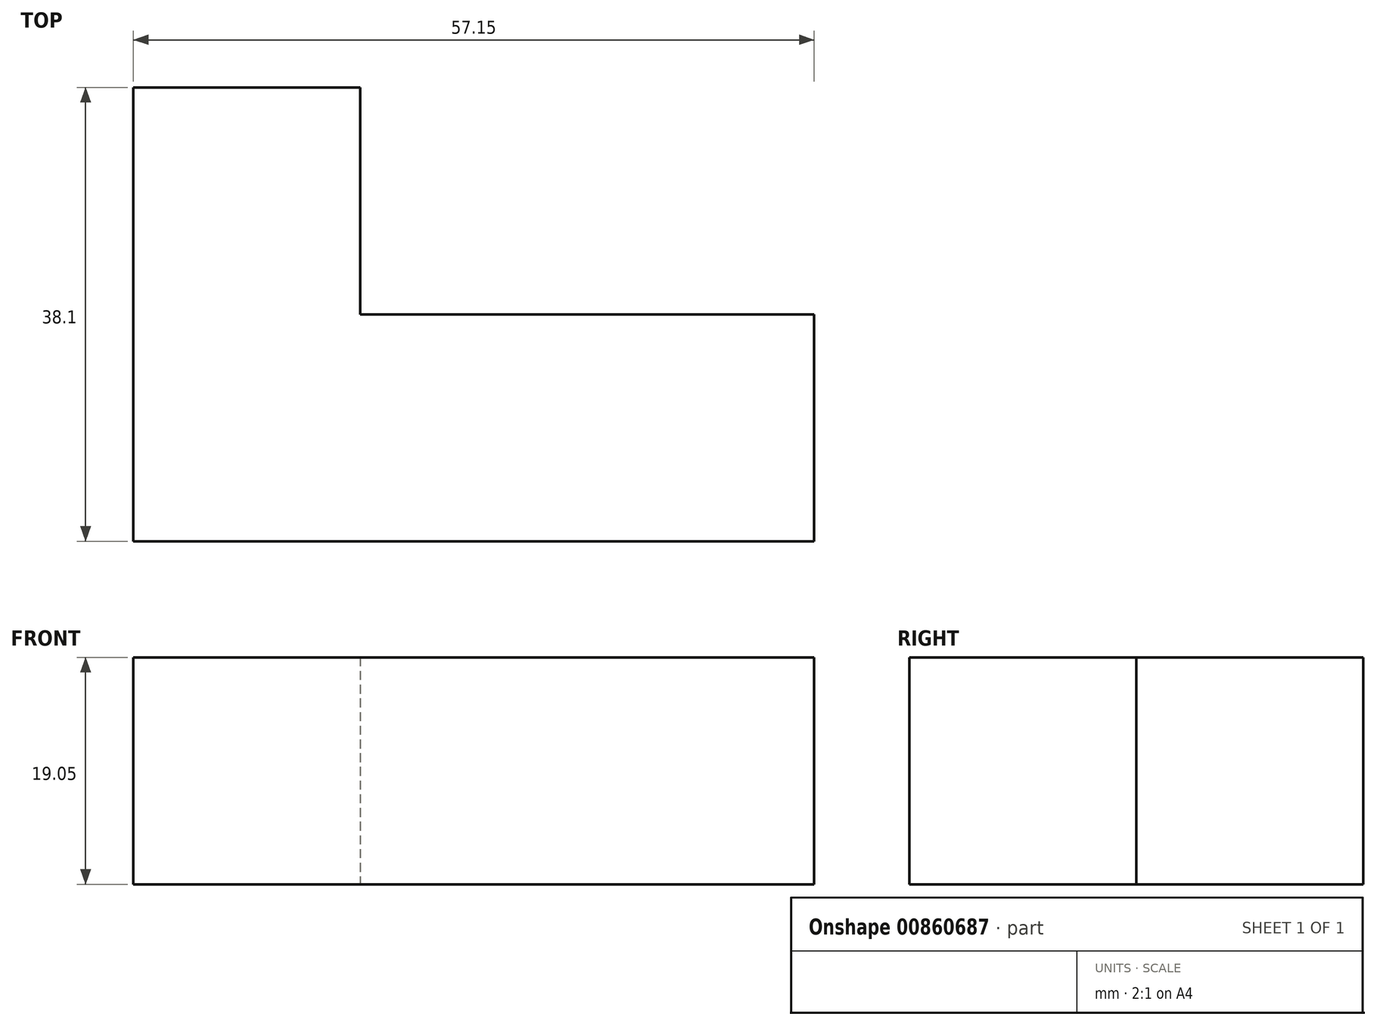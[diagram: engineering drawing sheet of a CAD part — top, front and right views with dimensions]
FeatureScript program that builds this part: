
annotation { "Feature Type Name" : "Feature", "Feature Type Description" : "" }
export const myFeature = defineFeature(function(context is Context, id is Id, definition is map)
    precondition{}
    {
        {
            var Q0;
            Q0=qCreatedBy(makeId("Top.planeOp"),FACE);
            var sketch = newSketch(context, id + "F0", { "sketchPlane" : qUnion([Q0])});
            skLineSegment(sketch, "E0", {"start": v(0, 0) * mm, "end": v(0, 38.1) * mm});
            skLineSegment(sketch, "E1", {"start": v(0, 38.1) * mm, "end": v(19.05, 38.1) * mm});
            skLineSegment(sketch, "E2", {"start": v(19.05, 38.1) * mm, "end": v(19.05, 19.05) * mm});
            skLineSegment(sketch, "E3", {"start": v(19.05, 19.05) * mm, "end": v(57.15, 19.05) * mm});
            skLineSegment(sketch, "E4", {"start": v(57.15, 19.05) * mm, "end": v(57.15, 0) * mm});
            skLineSegment(sketch, "E5", {"start": v(0, 0) * mm, "end": v(57.15, 0) * mm});
            skSolve(sketch);
        }
        {
            var Q0;
            Q0 = qSketchRegion(id + "F0", true);
            extrude(context, id + "F1", {"entities" : qUnion([Q0]), "depth" : 19.05 * mm, "offsetDistance" : 25.4 * mm});
        }
    });
